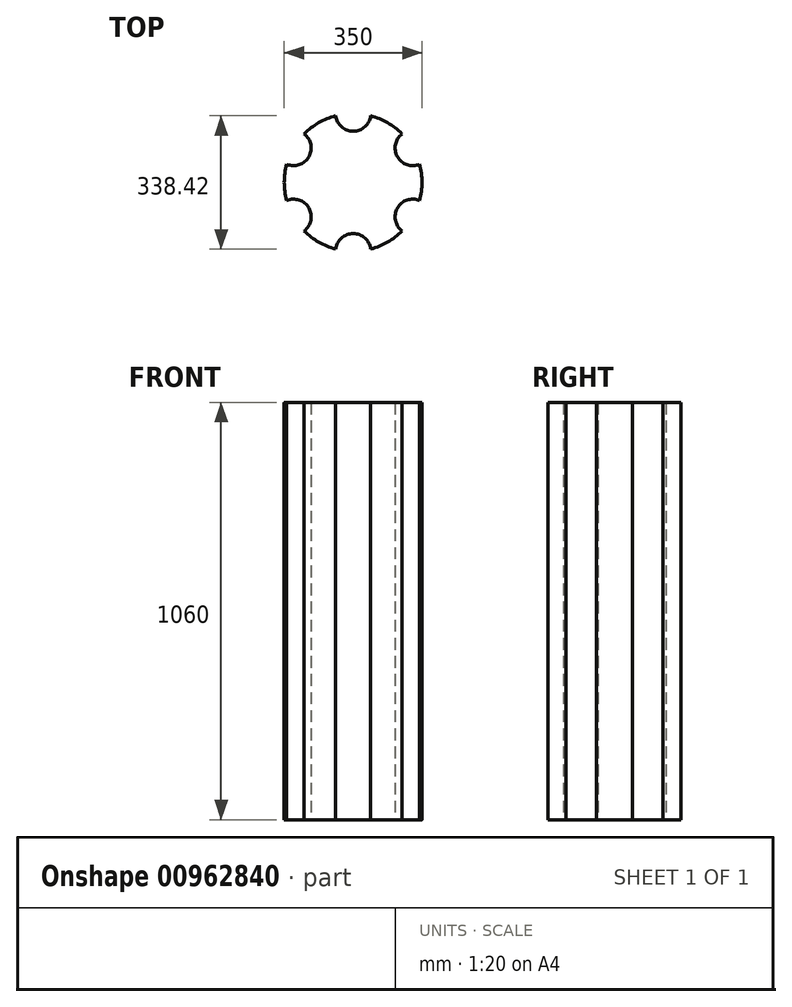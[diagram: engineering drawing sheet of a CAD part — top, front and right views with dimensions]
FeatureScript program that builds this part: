
annotation { "Feature Type Name" : "Feature", "Feature Type Description" : "" }
export const myFeature = defineFeature(function(context is Context, id is Id, definition is map)
    precondition{}
    {
        {
            var Q0;
            Q0=qCreatedBy(makeId("Top.planeOp"),FACE);
            var sketch = newSketch(context, id + "F0", { "sketchPlane" : qUnion([Q0])});
            skCircle(sketch, "E0", {"center": v(0, 0) * mm, "radius": 175 * mm});
            skLineSegment(sketch, "E1", {"start": v(-151.55, 87.5) * mm, "end": v(151.55, -87.5) * mm, "construction": true});
            skLineSegment(sketch, "E2", {"start": v(-151.55, -87.5) * mm, "end": v(151.55, 87.5) * mm, "construction": true});
            skLineSegment(sketch, "E3", {"start": v(0, 175) * mm, "end": v(0, -175) * mm, "construction": true});
            skCircle(sketch, "E4", {"center": v(-151.55, 87.5) * mm, "radius": 45 * mm});
            skCircle(sketch, "E5.1.0", {"center": v(-151.55, -87.5) * mm, "radius": 45 * mm});
            skCircle(sketch, "E5.2.0", {"center": v(0, -175) * mm, "radius": 45 * mm});
            skCircle(sketch, "E5.3.0", {"center": v(151.55, -87.5) * mm, "radius": 45 * mm});
            skCircle(sketch, "E5.4.0", {"center": v(151.55, 87.5) * mm, "radius": 45 * mm});
            skCircle(sketch, "E5.5.0", {"center": v(0, 175) * mm, "radius": 45 * mm});
            skSolve(sketch);
        }
        {
            var Q0;
            {var subQ1=sQuery(id+"F0.wireOp",EDGE,"E0");var subQ13=sQuery(id+"F0.wireOp",EDGE,"E5.4.0");var subQ15=makeQuery(id+"F0.imprint","INTERSECT",VERTEX,{"disambiguationData":[OD(0.0)],"derivedFrom":[subQ1,subQ13]});Q0=makeQuery(id+"F0.imprint","IMPRINT",FACE,{"disambiguationData":[TD([[makeQuery(id+"F0.imprint","IMPRINT",EDGE,{"disambiguationData":[TD([[subQ15,-1.0]])],"derivedFrom":subQ1}),1.0]])]});}
            extrude(context, id + "F1", {"entities" : qUnion([Q0]), "depth" : 1060 * mm, "offsetDistance" : 25 * mm});
        }
    });
